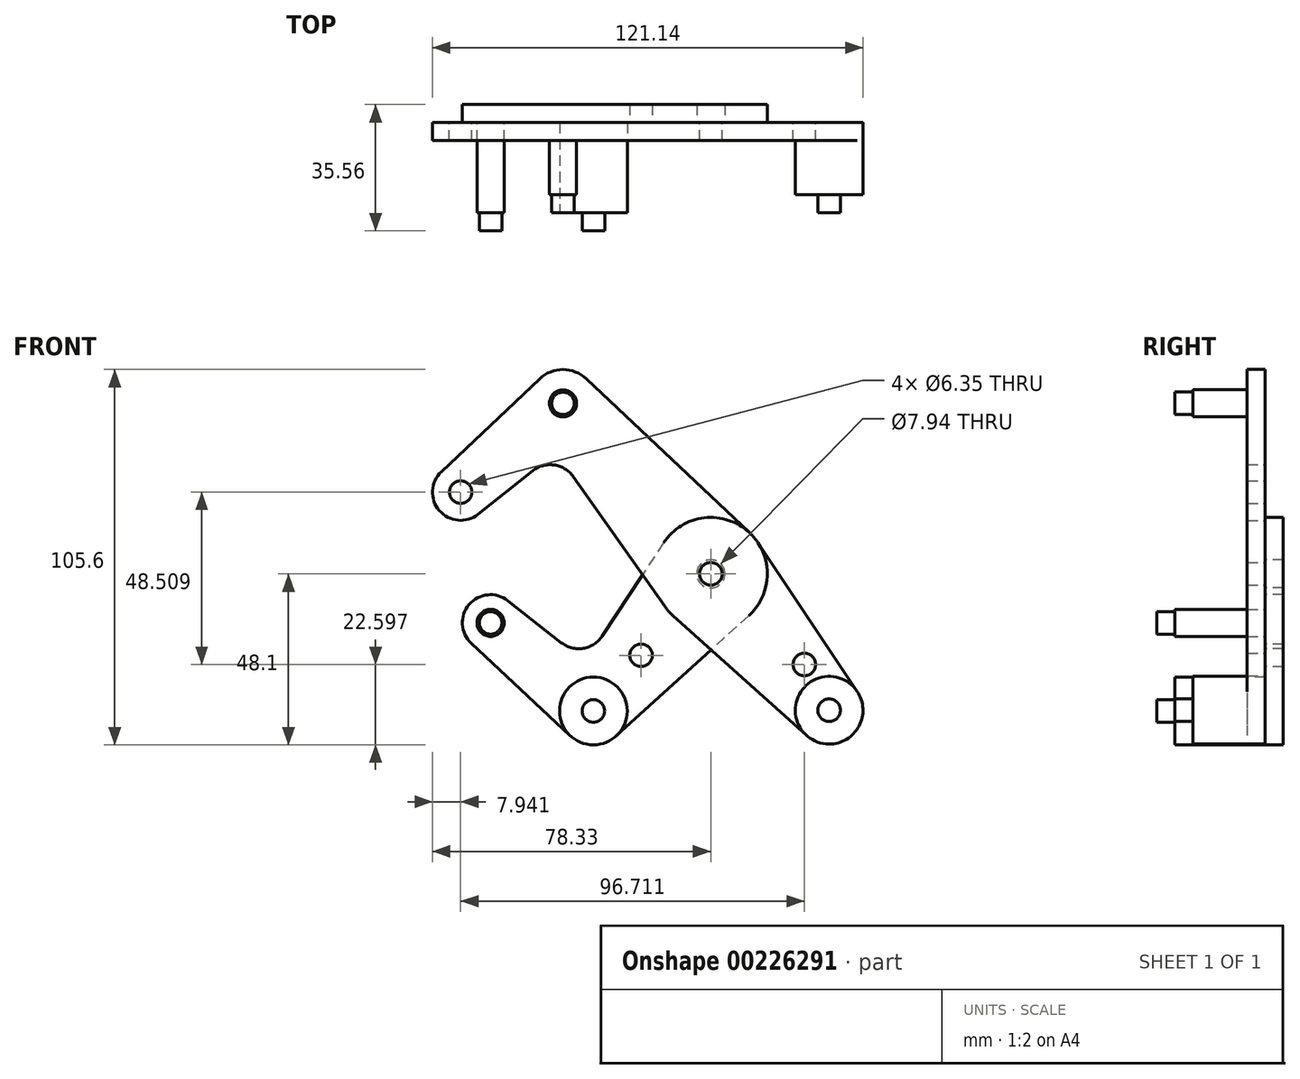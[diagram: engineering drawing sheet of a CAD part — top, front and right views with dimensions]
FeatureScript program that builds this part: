
annotation { "Feature Type Name" : "Feature", "Feature Type Description" : "" }
export const myFeature = defineFeature(function(context is Context, id is Id, definition is map)
    precondition{}
    {
        {
            var Q0;
            Q0=qCreatedBy(makeId("Front.planeOp"),FACE);
            var sketch = newSketch(context, id + "F0", { "sketchPlane" : qUnion([Q0])});
            skLineSegment(sketch, "E0", {"start": v(-41.6, 47.97) * mm, "end": v(41.6, -47.97) * mm, "construction": true});
            skCircle(sketch, "E1", {"center": v(0, 0) * mm, "radius": 3.18 * mm});
            skCircle(sketch, "E2", {"center": v(33.29, -38.38) * mm, "radius": 3.18 * mm});
            skCircle(sketch, "E3", {"center": v(-41.6, 47.97) * mm, "radius": 3.18 * mm});
            skCircle(sketch, "E4", {"center": v(-70.39, 23) * mm, "radius": 3.18 * mm});
            skLineSegment(sketch, "E5", {"start": v(-41.6, 47.97) * mm, "end": v(-70.39, 23) * mm, "construction": true});
            skCircle(sketch, "E6", {"center": v(33.29, -38.38) * mm, "radius": 9.53 * mm});
            skCircle(sketch, "E7", {"center": v(-70.39, 23) * mm, "radius": 7.94 * mm});
            skCircle(sketch, "E8", {"center": v(-41.6, 47.97) * mm, "radius": 9.53 * mm});
            skLineSegment(sketch, "E9", {"start": v(-75.83, 28.78) * mm, "end": v(-48.14, 54.9) * mm});
            skLineSegment(sketch, "E10", {"start": v(-65.44, 16.8) * mm, "end": v(-50.15, 28.98) * mm});
            skCircle(sketch, "E11", {"center": v(0, 0) * mm, "radius": 15.88 * mm});
            skLineSegment(sketch, "E12", {"start": v(-35.07, 54.9) * mm, "end": v(10.9, 11.55) * mm});
            skLineSegment(sketch, "E13", {"start": v(-38.72, 27.35) * mm, "end": v(-12.97, -9.15) * mm});
            skLineSegment(sketch, "E14", {"start": v(-10.6, -11.82) * mm, "end": v(26.93, -45.47) * mm});
            skLineSegment(sketch, "E15", {"start": v(13.2, 8.82) * mm, "end": v(41.2, -33.08) * mm});
            skArc(sketch, "E16.filletArc", {"start": v(-38.72, 27.35) * mm, "mid": v(-44.08, 30.63) * mm, "end": v(-50.15, 28.98) * mm});
            skLineSegment(sketch, "E17", {"start": v(0, 0) * mm, "end": v(-33.05, -38.58) * mm, "construction": true});
            skLineSegment(sketch, "E18", {"start": v(-33.05, -38.58) * mm, "end": v(-61.98, -13.8) * mm, "construction": true});
            skCircle(sketch, "E19", {"center": v(-61.98, -13.8) * mm, "radius": 3.18 * mm});
            skCircle(sketch, "E20", {"center": v(-33.05, -38.58) * mm, "radius": 3.18 * mm});
            skCircle(sketch, "E21", {"center": v(-61.98, -13.8) * mm, "radius": 7.94 * mm});
            skCircle(sketch, "E22", {"center": v(-33.05, -38.58) * mm, "radius": 9.53 * mm});
            skLineSegment(sketch, "E23", {"start": v(-57.08, -7.55) * mm, "end": v(-42.08, -19.35) * mm});
            skLineSegment(sketch, "E24", {"start": v(-67.4, -19.6) * mm, "end": v(-39.54, -45.55) * mm});
            skLineSegment(sketch, "E25", {"start": v(-13.25, 8.74) * mm, "end": v(-30.55, -17.48) * mm});
            skLineSegment(sketch, "E26", {"start": v(10.67, -11.75) * mm, "end": v(-26.65, -45.63) * mm});
            skArc(sketch, "E27.filletArc", {"start": v(-42.08, -19.35) * mm, "mid": v(-35.9, -20.95) * mm, "end": v(-30.55, -17.48) * mm});
            skCircle(sketch, "E28", {"center": v(-19.62, -22.9) * mm, "radius": 3.18 * mm});
            skCircle(sketch, "E29", {"center": v(26.32, -25.5) * mm, "radius": 3.18 * mm});
            skLineSegment(sketch, "E30", {"start": v(26.32, -25.5) * mm, "end": v(23.92, -27.58) * mm, "construction": true});
            skCircle(sketch, "E31", {"center": v(0, 0) * mm, "radius": 3.97 * mm});
            skSolve(sketch);
        }
        {
            var Q0;
            Q0=qCreatedBy(makeId("Front.planeOp"),FACE);
            cPlane(context, id + "F1", {"entities" : qUnion([Q0]), "cplaneType" : CPlaneType.OFFSET, "offset" : 12.7 * mm, "width" : 254 * mm, "height" : 254 * mm});
        }
        {
            var Q0;
            {var subQ1=sQuery(id+"F0.wireOp",EDGE,"E9");Q0=makeQuery(id+"F0.imprint","IMPRINT",FACE,{"disambiguationData":[TD([[makeQuery(id+"F0.imprint","IMPRINT",EDGE,{"derivedFrom":subQ1}),-1.0]])]});}
            var Q1;
            {var subQ0=sQuery(id+"F0.wireOp",EDGE,"E15");Q1=makeQuery(id+"F0.imprint","IMPRINT",FACE,{"disambiguationData":[TD([[makeQuery(id+"F0.imprint","IMPRINT",EDGE,{"derivedFrom":subQ0}),-1.0]])]});}
            var Q2;
            Q2=makeQuery(id+"F0.imprint","IMPRINT",FACE,{"disambiguationData":[TD([[makeQuery(id+"F0.imprint","IMPRINT",EDGE,{"derivedFrom":sQuery(id+"F0.wireOp",EDGE,"E2")}),-1.0]])]});
            var Q3;
            {var subQ0=sQuery(id+"F0.wireOp",EDGE,"E13");var subQ1=sQuery(id+"F0.wireOp",EDGE,"E11");var subQ2=makeQuery(id+"F0.imprint","INTERSECT",VERTEX,{"derivedFrom":[subQ1,subQ0]});Q3=makeQuery(id+"F0.imprint","IMPRINT",FACE,{"disambiguationData":[TD([[makeQuery(id+"F0.imprint","IMPRINT",EDGE,{"disambiguationData":[TD([[subQ2,1.0]])],"derivedFrom":subQ1}),-1.0]])]});}
            var Q4;
            {var subQ0=sQuery(id+"F0.wireOp",EDGE,"E14");var subQ1=sQuery(id+"F0.wireOp",EDGE,"E11");var subQ2=makeQuery(id+"F0.imprint","INTERSECT",VERTEX,{"derivedFrom":[subQ1,subQ0]});Q4=makeQuery(id+"F0.imprint","IMPRINT",FACE,{"disambiguationData":[TD([[makeQuery(id+"F0.imprint","IMPRINT",EDGE,{"disambiguationData":[TD([[subQ2,-1.0]])],"derivedFrom":subQ1}),-1.0]])]});}
            var Q5;
            Q5=makeQuery(id+"F0.imprint","IMPRINT",FACE,{"disambiguationData":[TD([[makeQuery(id+"F0.imprint","IMPRINT",EDGE,{"derivedFrom":sQuery(id+"F0.wireOp",EDGE,"E31")}),-1.0]])]});
            var Q6;
            Q6=makeQuery(id+"F0.imprint","IMPRINT",FACE,{"disambiguationData":[TD([[makeQuery(id+"F0.imprint","IMPRINT",EDGE,{"derivedFrom":sQuery(id+"F0.wireOp",EDGE,"E3")}),-1.0]])]});
            var Q7;
            Q7=makeQuery(id+"F0.imprint","IMPRINT",FACE,{"disambiguationData":[TD([[makeQuery(id+"F0.imprint","IMPRINT",EDGE,{"derivedFrom":sQuery(id+"F0.wireOp",EDGE,"E4")}),-1.0]])]});
            var Q8;
            Q8=makeQuery(id+"F0.imprint","IMPRINT",FACE,{"disambiguationData":[TD([[makeQuery(id+"F0.imprint","IMPRINT",EDGE,{"derivedFrom":sQuery(id+"F0.wireOp",EDGE,"E1")}),-1.0]])]});
            extrude(context, id + "F2", {"entities" : qUnion([Q0, Q1, Q2, Q3, Q4, Q5, Q6, Q7, Q8]), "depth" : 5.08 * mm});
        }
        {
            var Q0;
            Q0=makeQuery(id+"F0.imprint","IMPRINT",FACE,{"disambiguationData":[TD([[makeQuery(id+"F0.imprint","IMPRINT",EDGE,{"derivedFrom":sQuery(id+"F0.wireOp",EDGE,"E31")}),-1.0]])]});
            var Q1;
            {var subQ10=sQuery(id+"F0.wireOp",EDGE,"E23");Q1=makeQuery(id+"F0.imprint","IMPRINT",FACE,{"disambiguationData":[TD([[makeQuery(id+"F0.imprint","IMPRINT",EDGE,{"derivedFrom":subQ10}),-1.0]])]});}
            var Q2;
            Q2=makeQuery(id+"F0.imprint","IMPRINT",FACE,{"disambiguationData":[TD([[makeQuery(id+"F0.imprint","IMPRINT",EDGE,{"derivedFrom":sQuery(id+"F0.wireOp",EDGE,"E20")}),-1.0]])]});
            var Q3;
            Q3=makeQuery(id+"F0.imprint","IMPRINT",FACE,{"disambiguationData":[TD([[makeQuery(id+"F0.imprint","IMPRINT",EDGE,{"derivedFrom":sQuery(id+"F0.wireOp",EDGE,"E19")}),-1.0]])]});
            var Q4;
            {var subQ0=sQuery(id+"F0.wireOp",EDGE,"E14");var subQ1=sQuery(id+"F0.wireOp",EDGE,"E11");var subQ2=makeQuery(id+"F0.imprint","INTERSECT",VERTEX,{"derivedFrom":[subQ1,subQ0]});Q4=makeQuery(id+"F0.imprint","IMPRINT",FACE,{"disambiguationData":[TD([[makeQuery(id+"F0.imprint","IMPRINT",EDGE,{"disambiguationData":[TD([[subQ2,-1.0]])],"derivedFrom":subQ1}),-1.0]])]});}
            var Q5;
            {var subQ0=sQuery(id+"F0.wireOp",EDGE,"E13");var subQ1=sQuery(id+"F0.wireOp",EDGE,"E11");var subQ2=makeQuery(id+"F0.imprint","INTERSECT",VERTEX,{"derivedFrom":[subQ1,subQ0]});Q5=makeQuery(id+"F0.imprint","IMPRINT",FACE,{"disambiguationData":[TD([[makeQuery(id+"F0.imprint","IMPRINT",EDGE,{"disambiguationData":[TD([[subQ2,1.0]])],"derivedFrom":subQ1}),-1.0]])]});}
            extrude(context, id + "F3", {"entities" : qUnion([Q0, Q1, Q2, Q3, Q4, Q5]), "oppositeDirection" : true, "depth" : 5.08 * mm});
        }
        {
            var Q0;
            Q0=makeQuery(id+"F2.opExtrude","CAP_FACE",FACE,{"disambiguationData":[OSD([sQuery(id+"F0.wireOp",EDGE,"E1"),sQuery(id+"F0.wireOp",EDGE,"E2"),sQuery(id+"F0.wireOp",EDGE,"E3"),sQuery(id+"F0.wireOp",EDGE,"E4"),sQuery(id+"F0.wireOp",EDGE,"E6"),sQuery(id+"F0.wireOp",EDGE,"E7"),sQuery(id+"F0.wireOp",EDGE,"E8"),sQuery(id+"F0.wireOp",EDGE,"E9"),sQuery(id+"F0.wireOp",EDGE,"E10"),sQuery(id+"F0.wireOp",EDGE,"E11"),sQuery(id+"F0.wireOp",EDGE,"E12"),sQuery(id+"F0.wireOp",EDGE,"E13"),sQuery(id+"F0.wireOp",EDGE,"E14"),sQuery(id+"F0.wireOp",EDGE,"E15"),sQuery(id+"F0.wireOp",EDGE,"E16.filletArc"),sQuery(id+"F0.wireOp",EDGE,"E29")])],"isStart":true});
            var sketch = newSketch(context, id + "F4", { "sketchPlane" : qUnion([Q0])});
            skCircle(sketch, "E32.0", {"center": v(-33.29, -38.38) * mm, "radius": 9.53 * mm});
            skCircle(sketch, "E33", {"center": v(41.6, 47.97) * mm, "radius": 3.8 * mm});
            skSolve(sketch);
        }
        {
            var Q0;
            Q0=makeQuery(id+"F3.opExtrude","CAP_FACE",FACE,{"disambiguationData":[OSD([sQuery(id+"F0.wireOp",EDGE,"E11"),sQuery(id+"F0.wireOp",EDGE,"E19"),sQuery(id+"F0.wireOp",EDGE,"E20"),sQuery(id+"F0.wireOp",EDGE,"E21"),sQuery(id+"F0.wireOp",EDGE,"E22"),sQuery(id+"F0.wireOp",EDGE,"E23"),sQuery(id+"F0.wireOp",EDGE,"E24"),sQuery(id+"F0.wireOp",EDGE,"E25"),sQuery(id+"F0.wireOp",EDGE,"E26"),sQuery(id+"F0.wireOp",EDGE,"E27.filletArc"),sQuery(id+"F0.wireOp",EDGE,"E28"),sQuery(id+"F0.wireOp",EDGE,"E31")])],"isStart":false});
            var sketch = newSketch(context, id + "F5", { "sketchPlane" : qUnion([Q0])});
            skCircle(sketch, "E34.0", {"center": v(33.05, -38.58) * mm, "radius": 9.53 * mm});
            skCircle(sketch, "E35", {"center": v(61.98, -13.8) * mm, "radius": 3.8 * mm});
            skSolve(sketch);
        }
        {
            var Q0;
            Q0 = qSketchRegion(id + "F5", true);
            var Q1;
            Q1 = qSketchRegion(id + "F4", true);
            var Q2;
            Q2=qCreatedBy(id+"F1.planeOp",FACE);
            extrude(context, id + "F6", {"entities" : qUnion([Q0, Q1]), "endBound" : BoundingType.UP_TO_SURFACE, "oppositeDirection" : true, "endBoundEntityFace" : qUnion([Q2]), "depth" : 25.4 * mm});
        }
        {
            var Q0;
            Q0=makeQuery(id+"F2.opExtrude","SWEPT_BODY",BODY,{"disambiguationData":[OSD([sQuery(id+"F0.wireOp",EDGE,"E1"),sQuery(id+"F0.wireOp",EDGE,"E2"),sQuery(id+"F0.wireOp",EDGE,"E3"),sQuery(id+"F0.wireOp",EDGE,"E4"),sQuery(id+"F0.wireOp",EDGE,"E6"),sQuery(id+"F0.wireOp",EDGE,"E7"),sQuery(id+"F0.wireOp",EDGE,"E8"),sQuery(id+"F0.wireOp",EDGE,"E9"),sQuery(id+"F0.wireOp",EDGE,"E10"),sQuery(id+"F0.wireOp",EDGE,"E11"),sQuery(id+"F0.wireOp",EDGE,"E12"),sQuery(id+"F0.wireOp",EDGE,"E13"),sQuery(id+"F0.wireOp",EDGE,"E14"),sQuery(id+"F0.wireOp",EDGE,"E15"),sQuery(id+"F0.wireOp",EDGE,"E16.filletArc"),sQuery(id+"F0.wireOp",EDGE,"E29")])]});
            var Q1;
            Q1=makeQuery(id+"F3.opExtrude","SWEPT_BODY",BODY,{"disambiguationData":[OSD([sQuery(id+"F0.wireOp",EDGE,"E11"),sQuery(id+"F0.wireOp",EDGE,"E19"),sQuery(id+"F0.wireOp",EDGE,"E20"),sQuery(id+"F0.wireOp",EDGE,"E21"),sQuery(id+"F0.wireOp",EDGE,"E22"),sQuery(id+"F0.wireOp",EDGE,"E23"),sQuery(id+"F0.wireOp",EDGE,"E24"),sQuery(id+"F0.wireOp",EDGE,"E25"),sQuery(id+"F0.wireOp",EDGE,"E26"),sQuery(id+"F0.wireOp",EDGE,"E27.filletArc"),sQuery(id+"F0.wireOp",EDGE,"E28"),sQuery(id+"F0.wireOp",EDGE,"E31")])]});
            var Q2;
            Q2=makeQuery(id+"F6.opExtrude","SWEPT_BODY",BODY,{"disambiguationData":[OSD([sQuery(id+"F4.wireOp",EDGE,"E33")])]});
            var Q3;
            Q3=makeQuery(id+"F6.opExtrude","SWEPT_BODY",BODY,{"disambiguationData":[OSD([sQuery(id+"F5.wireOp",EDGE,"E35")])]});
            var Q4;
            Q4=makeQuery(id+"F6.opExtrude","SWEPT_BODY",BODY,{"disambiguationData":[OSD([sQuery(id+"F5.wireOp",EDGE,"E34.0")])]});
            var Q5;
            Q5=makeQuery(id+"F6.opExtrude","SWEPT_BODY",BODY,{"disambiguationData":[OSD([sQuery(id+"F4.wireOp",EDGE,"E32.0")])]});
            booleanBodies(context, id + "F7", {"operationType" : BooleanOperationType.SUBTRACTION, "tools" : qUnion([Q0, Q1]), "targets" : qUnion([Q2, Q3, Q4, Q5]), "keepTools" : true});
        }
        {
            var Q0;
            Q0=makeQuery(id+"F6.opExtrude","SWEPT_BODY",BODY,{"disambiguationData":[OSD([sQuery(id+"F5.wireOp",EDGE,"E35")])]});
            var Q1;
            Q1=makeQuery(id+"F6.opExtrude","SWEPT_BODY",BODY,{"disambiguationData":[OSD([sQuery(id+"F4.wireOp",EDGE,"E33")])]});
            var Q2;
            Q2=makeQuery(id+"F6.opExtrude","SWEPT_BODY",BODY,{"disambiguationData":[OSD([sQuery(id+"F4.wireOp",EDGE,"E32.0")])]});
            var Q3;
            Q3=makeQuery(id+"F6.opExtrude","SWEPT_BODY",BODY,{"disambiguationData":[OSD([sQuery(id+"F5.wireOp",EDGE,"E34.0")])]});
            var Q4;
            Q4=qCreatedBy(id+"F1.planeOp",FACE);
            mirror(context, id + "F8", {"operationType" : NewBodyOperationType.ADD, "entities" : qUnion([Q0, Q1, Q2, Q3]), "mirrorPlane" : qUnion([Q4])});
        }
    });
